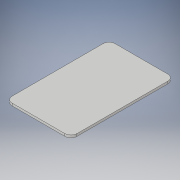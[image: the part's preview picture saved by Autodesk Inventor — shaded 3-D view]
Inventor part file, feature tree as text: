
AUTODESK INVENTOR PART (.ipt)
format: ipt  version: 2018 (Build 220112000, 112)  size: 99,840 bytes
history: native  units: in
note: dims shown in document units (in); Inventor stores cm internally (conversion verified against a paired STEP export)
features: extrude x1, fillet x1, sketch x1
ambient origin geometry x8: Origin, YZ Plane, XZ Plane, XY Plane, X Axis, Y Axis, Z Axis, Center Point
bodies: Solid1 (feature_tree)
feature tree (3):
  extrude  "Extrusion1"  Depth=2.125in
  fillet  "Fillet1"  Radius=0.0787in
  sketch  "Sketch1"  dims[d0=3.375in d1=2.125in d2=0.0787in d3=0.0in d4=0.1969in]
